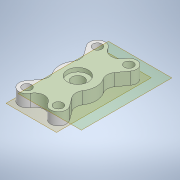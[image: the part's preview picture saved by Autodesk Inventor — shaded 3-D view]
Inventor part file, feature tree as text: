
AUTODESK INVENTOR PART (.ipt)
format: ipt  version: 2022 (Build 260153000, 153)  size: 232,960 bytes
history: native  units: mm
features: reference x6, other x5, plane x4, sketch x3, extrude x3
ambient origin geometry x8: Origin, YZ Plane, XZ Plane, XY Plane, X Axis, Y Axis, Z Axis, Center Point
bodies: Solid1 (feature_tree)
feature tree (21):
  plane  "Work Plane1"
  sketch  "Sketch1"  dims[d1=0.3mm d2=0.3mm]
  plane  "Work Plane2"
  extrude  "Extrusion1"  Depth=0.3mm
  sketch  "Sketch3"  dims[d3=10.0mm d4=0.0mm d8=0.3mm]
  plane  "Work Plane4"
  extrude  "Extrusion3"  Depth=10.0mm
  extrude  "Extrusion4"  Depth=0.1mm
  plane  "Work Plane5"
  reference  "Reference1"
  reference  "Reference2"
  reference  "Reference3"
  reference  "Reference5"
  sketch  "Sketch4"  dims[d9=0.3mm d11=0.3mm d12=10.0mm d13=0.0mm d14=0.1mm d15=0.0mm d20=0.3mm]
  reference  "Reference7"
  reference  "Reference8"
  other  "<userpath>\OneDrive - Imperial College London\ROBOICP MK2\solids feeder assembly.iam"
  other  "solids feeder assembly.iam"
  other  "screw_casing:1"
  other  "smol stepper:1"
  other  "Screw Shaft:1"
